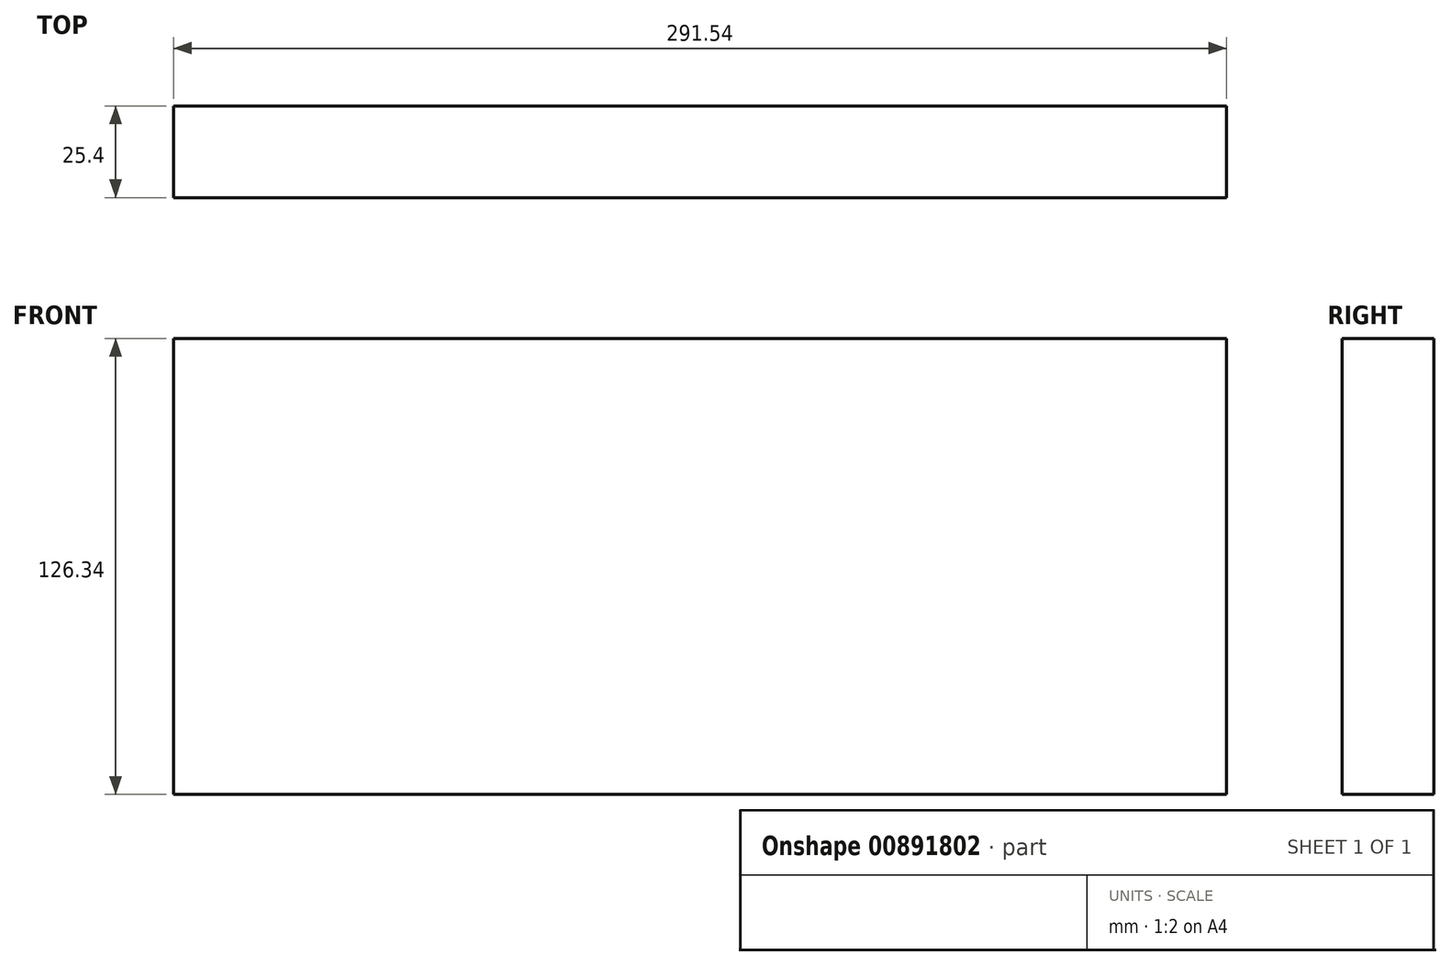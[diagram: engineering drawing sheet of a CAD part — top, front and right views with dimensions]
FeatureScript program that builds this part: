
annotation { "Feature Type Name" : "Feature", "Feature Type Description" : "" }
export const myFeature = defineFeature(function(context is Context, id is Id, definition is map)
    precondition{}
    {
        {
            var Q0;
            Q0=qCreatedBy(makeId("Front.planeOp"),FACE);
            var sketch = newSketch(context, id + "F0", { "sketchPlane" : qUnion([Q0])});
            skLineSegment(sketch, "E0.bottom", {"start": v(-57.36, 49.29) * mm, "end": v(-348.9, 49.29) * mm});
            skLineSegment(sketch, "E0.top", {"start": v(-57.36, -77.05) * mm, "end": v(-348.9, -77.05) * mm});
            skLineSegment(sketch, "E0.left", {"start": v(-57.36, 49.29) * mm, "end": v(-57.36, -77.05) * mm});
            skLineSegment(sketch, "E0.right", {"start": v(-348.9, 49.29) * mm, "end": v(-348.9, -77.05) * mm});
            skSolve(sketch);
        }
        {
            var Q0;
            Q0=makeQuery(id+"F0.imprint","IMPRINT",FACE,{"disambiguationData":[TD([[makeQuery(id+"F0.imprint","IMPRINT",EDGE,{"derivedFrom":sQuery(id+"F0.wireOp",EDGE,"E0.bottom")}),1.0]])]});
            extrude(context, id + "F1", {"entities" : qUnion([Q0]), "depth" : 25.4 * mm, "offsetDistance" : 25.4 * mm});
        }
    });
